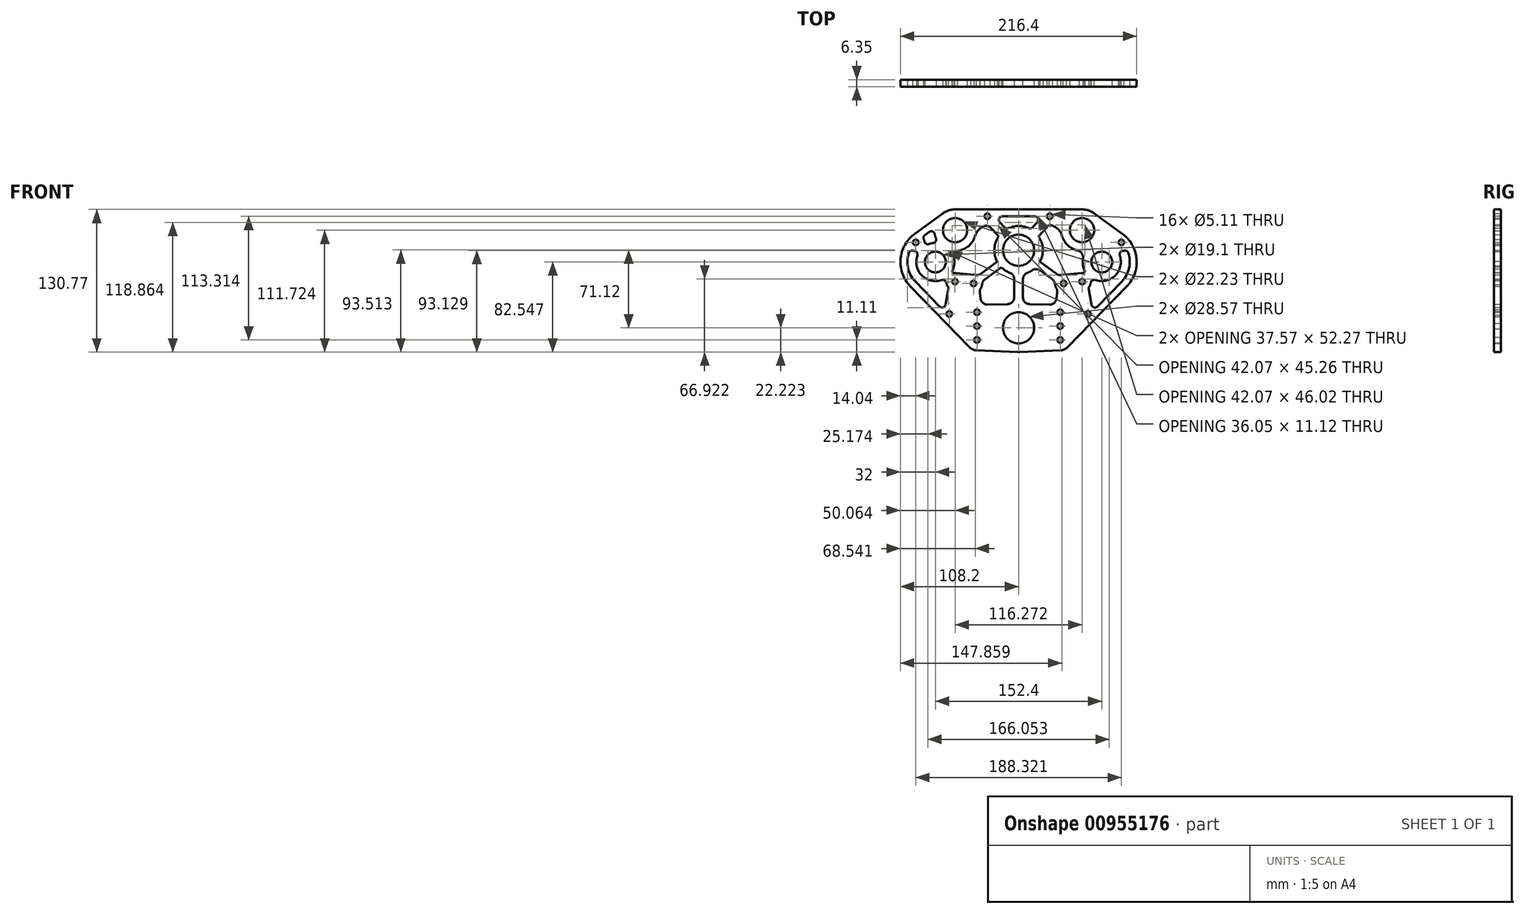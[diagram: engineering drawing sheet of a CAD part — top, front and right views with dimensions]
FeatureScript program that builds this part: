
annotation { "Feature Type Name" : "Feature", "Feature Type Description" : "" }
export const myFeature = defineFeature(function(context is Context, id is Id, definition is map)
    precondition{}
    {
        {
            var Q0;
            Q0=qCreatedBy(makeId("Front.planeOp"),FACE);
            var sketch = newSketch(context, id + "F0", { "sketchPlane" : qUnion([Q0])});
            skCircle(sketch, "E0", {"center": v(-76.2, 58.74) * mm, "radius": 32 * mm, "construction": true});
            skCircle(sketch, "E1", {"center": v(76.2, 58.74) * mm, "radius": 32 * mm, "construction": true});
            skLineSegment(sketch, "E2", {"start": v(-76.2, 58.74) * mm, "end": v(76.2, 58.74) * mm, "construction": true});
            skLineSegment(sketch, "E3", {"start": v(0, 58.74) * mm, "end": v(0, 0) * mm, "construction": true});
            skCircle(sketch, "E4", {"center": v(-76.2, 58.74) * mm, "radius": 7.63 * mm, "construction": true});
            skCircle(sketch, "E5", {"center": v(76.2, 58.74) * mm, "radius": 7.63 * mm, "construction": true});
            skLineSegment(sketch, "E6.bottom", {"start": v(-127, 23.81) * mm, "end": v(127, 23.81) * mm, "construction": true});
            skLineSegment(sketch, "E6.top", {"start": v(-127, -26.99) * mm, "end": v(127, -26.99) * mm, "construction": true});
            skLineSegment(sketch, "E6.left", {"start": v(-127, 23.81) * mm, "end": v(-127, -26.99) * mm, "construction": true});
            skLineSegment(sketch, "E6.right", {"start": v(127, 23.81) * mm, "end": v(127, -26.99) * mm, "construction": true});
            skPoint(sketch, "E6.middle", {"position": v(0, -1.59) * mm});
            skCircle(sketch, "E7", {"center": v(0, 0) * mm, "radius": 50.8 * mm, "construction": true});
            skCircle(sketch, "E8", {"center": v(-58.14, 87.91) * mm, "radius": 26.68 * mm, "construction": true});
            skCircle(sketch, "E9", {"center": v(58.14, 87.91) * mm, "radius": 26.68 * mm, "construction": true});
            skCircle(sketch, "E10", {"center": v(0, 69.53) * mm, "radius": 34.3 * mm, "construction": true});
            skCircle(sketch, "E11", {"center": v(0, 69.53) * mm, "radius": 25.4 * mm, "construction": true});
            skCircle(sketch, "E12", {"center": v(0, 69.53) * mm, "radius": 38.1 * mm, "construction": true});
            skCircle(sketch, "E13", {"center": v(0, -1.59) * mm, "radius": 33.02 * mm, "construction": true});
            skCircle(sketch, "E14", {"center": v(0, -1.59) * mm, "radius": 45.72 * mm, "construction": true});
            skCircle(sketch, "E15", {"center": v(-76.2, 58.74) * mm, "radius": 9.55 * mm});
            skCircle(sketch, "E16", {"center": v(76.2, 58.74) * mm, "radius": 9.55 * mm});
            skCircle(sketch, "E17", {"center": v(-58.14, 87.91) * mm, "radius": 11.11 * mm});
            skCircle(sketch, "E18", {"center": v(58.14, 87.91) * mm, "radius": 11.11 * mm});
            skCircle(sketch, "E19", {"center": v(0, 69.53) * mm, "radius": 14.29 * mm});
            skCircle(sketch, "E20", {"center": v(0, -1.59) * mm, "radius": 14.29 * mm});
            skCircle(sketch, "E21", {"center": v(-38.1, 12.7) * mm, "radius": 9.53 * mm, "construction": true});
            skCircle(sketch, "E22", {"center": v(-38.1, -12.7) * mm, "radius": 9.53 * mm, "construction": true});
            skCircle(sketch, "E23", {"center": v(38.1, -12.7) * mm, "radius": 9.53 * mm, "construction": true});
            skCircle(sketch, "E24", {"center": v(38.1, 12.7) * mm, "radius": 9.53 * mm, "construction": true});
            skCircle(sketch, "E25", {"center": v(38.1, 0) * mm, "radius": 9.53 * mm, "construction": true});
            skCircle(sketch, "E26", {"center": v(-38.1, 0) * mm, "radius": 9.53 * mm, "construction": true});
            skCircle(sketch, "E27", {"center": v(38.1, -12.7) * mm, "radius": 2.55 * mm});
            skCircle(sketch, "E28", {"center": v(38.1, 0) * mm, "radius": 2.55 * mm});
            skCircle(sketch, "E29", {"center": v(38.1, 12.7) * mm, "radius": 2.55 * mm});
            skCircle(sketch, "E30", {"center": v(-38.1, 12.7) * mm, "radius": 2.55 * mm});
            skCircle(sketch, "E31", {"center": v(-38.1, 0) * mm, "radius": 2.55 * mm});
            skCircle(sketch, "E32", {"center": v(-38.1, -12.7) * mm, "radius": 2.55 * mm});
            skLineSegment(sketch, "E33", {"start": v(-44.93, -19.34) * mm, "end": v(-99.15, 36.43) * mm});
            skArc(sketch, "E34", {"start": v(-44.93, -19.34) * mm, "mid": v(-42, -21.4) * mm, "end": v(-38.5, -22.22) * mm});
            skArc(sketch, "E35", {"start": v(38.5, -22.22) * mm, "mid": v(42, -21.4) * mm, "end": v(44.93, -19.34) * mm});
            skLineSegment(sketch, "E36", {"start": v(44.93, -19.34) * mm, "end": v(99.15, 36.43) * mm});
            skCircle(sketch, "E37", {"center": v(58.14, 87.91) * mm, "radius": 19.05 * mm, "construction": true});
            skCircle(sketch, "E38", {"center": v(-58.14, 87.91) * mm, "radius": 19.05 * mm, "construction": true});
            skArc(sketch, "E39", {"start": v(99.15, 36.43) * mm, "mid": v(108.09, 61.46) * mm, "end": v(95.04, 84.61) * mm});
            skArc(sketch, "E40", {"start": v(-95.04, 84.61) * mm, "mid": v(-108.09, 61.46) * mm, "end": v(-99.15, 36.43) * mm});
            skLineSegment(sketch, "E41", {"start": v(-58.24, 40.78) * mm, "end": v(-76.2, 58.74) * mm, "construction": true});
            skLineSegment(sketch, "E42", {"start": v(-76.2, 58.74) * mm, "end": v(-94.16, 76.7) * mm, "construction": true});
            skCircle(sketch, "E43", {"center": v(-94.16, 76.7) * mm, "radius": 2.55 * mm});
            skCircle(sketch, "E44", {"center": v(-58.24, 40.78) * mm, "radius": 2.55 * mm});
            skCircle(sketch, "E45.MirrorC", {"center": v(58.24, 40.78) * mm, "radius": 2.55 * mm});
            skLineSegment(sketch, "E46.MirrorCS", {"start": v(58.24, 40.78) * mm, "end": v(76.2, 58.74) * mm, "construction": true});
            skLineSegment(sketch, "E47.MirrorCS", {"start": v(76.2, 58.74) * mm, "end": v(94.16, 76.7) * mm, "construction": true});
            skCircle(sketch, "E48.MirrorC", {"center": v(94.16, 76.7) * mm, "radius": 2.55 * mm});
            skLineSegment(sketch, "E49", {"start": v(95.04, 84.61) * mm, "end": v(69.35, 103.31) * mm});
            skLineSegment(sketch, "E50", {"start": v(-95.04, 84.61) * mm, "end": v(-69.35, 103.31) * mm});
            skLineSegment(sketch, "E51", {"start": v(-58.14, 106.96) * mm, "end": v(58.14, 106.96) * mm});
            skArc(sketch, "E52", {"start": v(-69.35, 103.31) * mm, "mid": v(-64.03, 106.03) * mm, "end": v(-58.14, 106.96) * mm});
            skArc(sketch, "E53", {"start": v(58.14, 106.96) * mm, "mid": v(64.03, 106.03) * mm, "end": v(69.35, 103.31) * mm});
            skCircle(sketch, "E54", {"center": v(0, -1.59) * mm, "radius": 22.23 * mm, "construction": true});
            skLineSegment(sketch, "E55", {"start": v(38.5, -22.22) * mm, "end": v(0.93, -23.8) * mm});
            skLineSegment(sketch, "E56", {"start": v(-38.5, -22.22) * mm, "end": v(-0.93, -23.8) * mm});
            skArc(sketch, "E57", {"start": v(-0.93, -23.8) * mm, "mid": v(0, -23.81) * mm, "end": v(0.93, -23.8) * mm});
            skLineSegment(sketch, "E58.bottom", {"start": v(-38.1, -12.7) * mm, "end": v(38.1, -12.7) * mm, "construction": true});
            skLineSegment(sketch, "E58.top", {"start": v(-38.1, 12.7) * mm, "end": v(38.1, 12.7) * mm, "construction": true});
            skLineSegment(sketch, "E58.left", {"start": v(-38.1, -12.7) * mm, "end": v(-38.1, 12.7) * mm, "construction": true});
            skLineSegment(sketch, "E58.right", {"start": v(38.1, -12.7) * mm, "end": v(38.1, 12.7) * mm, "construction": true});
            skCircle(sketch, "E59", {"center": v(-28.58, 100.61) * mm, "radius": 6.35 * mm, "construction": true});
            skCircle(sketch, "E60", {"center": v(-28.58, 100.61) * mm, "radius": 2.55 * mm});
            skCircle(sketch, "E61.MirrorC", {"center": v(28.57, 100.61) * mm, "radius": 6.35 * mm, "construction": true});
            skCircle(sketch, "E62.MirrorC", {"center": v(28.57, 100.61) * mm, "radius": 2.55 * mm});
            skCircle(sketch, "E63", {"center": v(-63.5, 11.15) * mm, "radius": 7.94 * mm, "construction": true});
            skCircle(sketch, "E64", {"center": v(-63.5, 11.15) * mm, "radius": 2.55 * mm});
            skCircle(sketch, "E65.MirrorC", {"center": v(63.5, 11.15) * mm, "radius": 7.94 * mm, "construction": true});
            skCircle(sketch, "E66.MirrorC", {"center": v(63.5, 11.15) * mm, "radius": 2.55 * mm});
            skCircle(sketch, "E67", {"center": v(-41.28, 39.05) * mm, "radius": 6.35 * mm, "construction": true});
            skCircle(sketch, "E68", {"center": v(41.28, 39.05) * mm, "radius": 6.35 * mm, "construction": true});
            skCircle(sketch, "E69", {"center": v(41.28, 39.05) * mm, "radius": 2.55 * mm});
            skCircle(sketch, "E70", {"center": v(-41.28, 39.05) * mm, "radius": 2.55 * mm});
            skLineSegment(sketch, "E71", {"start": v(41.28, 39.05) * mm, "end": v(-41.28, 39.05) * mm, "construction": true});
            skLineSegment(sketch, "E72", {"start": v(0, 39.05) * mm, "end": v(0, 69.53) * mm, "construction": true});
            skSolve(sketch);
        }
        {
            var Q0;
            Q0=qSketchRegion(id+"F0",true);
            extrude(context, id + "F1", {"entities" : qUnion([Q0]), "depth" : 6.35 * mm, "offsetDistance" : 25.4 * mm});
        }
        {
            var Q0;
            Q0=makeQuery(id+"F1.opExtrude","CAP_FACE",FACE,{"disambiguationData":[OSD([sQuery(id+"F0.wireOp",EDGE,"E15"),sQuery(id+"F0.wireOp",EDGE,"E16"),sQuery(id+"F0.wireOp",EDGE,"E17"),sQuery(id+"F0.wireOp",EDGE,"E18"),sQuery(id+"F0.wireOp",EDGE,"E19"),sQuery(id+"F0.wireOp",EDGE,"E20"),sQuery(id+"F0.wireOp",EDGE,"E27"),sQuery(id+"F0.wireOp",EDGE,"E28"),sQuery(id+"F0.wireOp",EDGE,"E29"),sQuery(id+"F0.wireOp",EDGE,"E30"),sQuery(id+"F0.wireOp",EDGE,"E31"),sQuery(id+"F0.wireOp",EDGE,"E32"),sQuery(id+"F0.wireOp",EDGE,"E33"),sQuery(id+"F0.wireOp",EDGE,"E34"),sQuery(id+"F0.wireOp",EDGE,"E35"),sQuery(id+"F0.wireOp",EDGE,"E36"),sQuery(id+"F0.wireOp",EDGE,"E39"),sQuery(id+"F0.wireOp",EDGE,"E40"),sQuery(id+"F0.wireOp",EDGE,"E43"),sQuery(id+"F0.wireOp",EDGE,"E44"),sQuery(id+"F0.wireOp",EDGE,"E45.MirrorC"),sQuery(id+"F0.wireOp",EDGE,"E48.MirrorC"),sQuery(id+"F0.wireOp",EDGE,"E49"),sQuery(id+"F0.wireOp",EDGE,"E50"),sQuery(id+"F0.wireOp",EDGE,"E51"),sQuery(id+"F0.wireOp",EDGE,"E52"),sQuery(id+"F0.wireOp",EDGE,"E53"),sQuery(id+"F0.wireOp",EDGE,"E55"),sQuery(id+"F0.wireOp",EDGE,"E56"),sQuery(id+"F0.wireOp",EDGE,"E57"),sQuery(id+"F0.wireOp",EDGE,"E60"),sQuery(id+"F0.wireOp",EDGE,"E62.MirrorC"),sQuery(id+"F0.wireOp",EDGE,"E64"),sQuery(id+"F0.wireOp",EDGE,"E66.MirrorC"),sQuery(id+"F0.wireOp",EDGE,"E69"),sQuery(id+"F0.wireOp",EDGE,"E70")])],"isStart":false});
            var sketch = newSketch(context, id + "F2", { "sketchPlane" : qUnion([Q0])});
            skCircle(sketch, "E73", {"center": v(-58.14, 87.91) * mm, "radius": 19.05 * mm, "construction": true});
            skCircle(sketch, "E74", {"center": v(0, 69.53) * mm, "radius": 22.23 * mm, "construction": true});
            skCircle(sketch, "E75", {"center": v(58.14, 87.91) * mm, "radius": 19.05 * mm, "construction": true});
            skCircle(sketch, "E76", {"center": v(76.2, 58.74) * mm, "radius": 17.49 * mm, "construction": true});
            skCircle(sketch, "E77", {"center": v(94.16, 76.7) * mm, "radius": 7.94 * mm, "construction": true});
            skCircle(sketch, "E78", {"center": v(58.24, 40.78) * mm, "radius": 7.94 * mm, "construction": true});
            skCircle(sketch, "E79", {"center": v(41.28, 39.05) * mm, "radius": 7.94 * mm, "construction": true});
            skCircle(sketch, "E80", {"center": v(63.5, 11.15) * mm, "radius": 7.94 * mm, "construction": true});
            skCircle(sketch, "E81", {"center": v(38.1, 12.7) * mm, "radius": 7.94 * mm, "construction": true});
            skCircle(sketch, "E82", {"center": v(38.1, 0) * mm, "radius": 7.94 * mm, "construction": true});
            skCircle(sketch, "E83", {"center": v(38.1, -12.7) * mm, "radius": 7.94 * mm, "construction": true});
            skCircle(sketch, "E84", {"center": v(-38.1, 12.7) * mm, "radius": 7.94 * mm, "construction": true});
            skCircle(sketch, "E85", {"center": v(-38.1, 0) * mm, "radius": 7.94 * mm, "construction": true});
            skCircle(sketch, "E86", {"center": v(-38.1, -12.7) * mm, "radius": 7.94 * mm, "construction": true});
            skCircle(sketch, "E87", {"center": v(-63.5, 11.15) * mm, "radius": 7.94 * mm, "construction": true});
            skCircle(sketch, "E88", {"center": v(-41.28, 39.05) * mm, "radius": 7.94 * mm, "construction": true});
            skCircle(sketch, "E89", {"center": v(-58.24, 40.78) * mm, "radius": 7.94 * mm, "construction": true});
            skCircle(sketch, "E90", {"center": v(-76.2, 58.74) * mm, "radius": 17.49 * mm, "construction": true});
            skCircle(sketch, "E91", {"center": v(-94.16, 76.7) * mm, "radius": 7.94 * mm, "construction": true});
            skCircle(sketch, "E92", {"center": v(-28.58, 100.61) * mm, "radius": 7.94 * mm, "construction": true});
            skCircle(sketch, "E93", {"center": v(28.57, 100.61) * mm, "radius": 7.94 * mm, "construction": true});
            skCircle(sketch, "E94", {"center": v(0, -1.59) * mm, "radius": 22.23 * mm, "construction": true});
            skLineSegment(sketch, "E95", {"start": v(-99.15, 36.43) * mm, "end": v(-44.93, -19.34) * mm, "construction": true});
            skLineSegment(sketch, "E96", {"start": v(-38.5, -22.22) * mm, "end": v(-0.93, -23.8) * mm, "construction": true});
            skLineSegment(sketch, "E97", {"start": v(0.93, -23.8) * mm, "end": v(38.5, -22.22) * mm, "construction": true});
            skLineSegment(sketch, "E98", {"start": v(44.93, -19.34) * mm, "end": v(99.15, 36.43) * mm, "construction": true});
            skLineSegment(sketch, "E99", {"start": v(95.04, 84.61) * mm, "end": v(69.35, 103.31) * mm, "construction": true});
            skLineSegment(sketch, "E100", {"start": v(58.14, 106.96) * mm, "end": v(-58.14, 106.96) * mm, "construction": true});
            skLineSegment(sketch, "E101", {"start": v(-69.35, 103.31) * mm, "end": v(-95.04, 84.61) * mm, "construction": true});
            skArc(sketch, "E102", {"start": v(-58.14, 106.96) * mm, "mid": v(-64.03, 106.03) * mm, "end": v(-69.35, 103.31) * mm, "construction": true});
            skArc(sketch, "E103", {"start": v(-95.04, 84.61) * mm, "mid": v(-108.09, 61.46) * mm, "end": v(-99.15, 36.43) * mm, "construction": true});
            skArc(sketch, "E104", {"start": v(-44.93, -19.34) * mm, "mid": v(-42, -21.4) * mm, "end": v(-38.5, -22.22) * mm, "construction": true});
            skArc(sketch, "E105", {"start": v(-0.93, -23.8) * mm, "mid": v(0, -23.81) * mm, "end": v(0.93, -23.8) * mm, "construction": true});
            skArc(sketch, "E106", {"start": v(38.5, -22.22) * mm, "mid": v(42, -21.4) * mm, "end": v(44.93, -19.34) * mm, "construction": true});
            skArc(sketch, "E107", {"start": v(99.15, 36.43) * mm, "mid": v(108.09, 61.46) * mm, "end": v(95.04, 84.61) * mm, "construction": true});
            skLineSegment(sketch, "E108.0", {"start": v(58.14, 100.61) * mm, "end": v(-58.14, 100.61) * mm, "construction": true});
            skArc(sketch, "E108.1", {"start": v(58.14, 100.61) * mm, "mid": v(62.07, 99.99) * mm, "end": v(65.61, 98.18) * mm, "construction": true});
            skLineSegment(sketch, "E108.2", {"start": v(91.3, 79.48) * mm, "end": v(65.61, 98.18) * mm, "construction": true});
            skArc(sketch, "E108.3", {"start": v(-40.38, -14.91) * mm, "mid": v(-39.4, -15.6) * mm, "end": v(-38.23, -15.87) * mm, "construction": true});
            skLineSegment(sketch, "E108.4", {"start": v(-94.6, 40.85) * mm, "end": v(-40.38, -14.91) * mm, "construction": true});
            skArc(sketch, "E108.5", {"start": v(-91.3, 79.48) * mm, "mid": v(-101.76, 60.92) * mm, "end": v(-94.6, 40.85) * mm, "construction": true});
            skLineSegment(sketch, "E108.6", {"start": v(-65.61, 98.18) * mm, "end": v(-91.3, 79.48) * mm, "construction": true});
            skLineSegment(sketch, "E108.7", {"start": v(-38.23, -15.87) * mm, "end": v(-0.67, -17.45) * mm, "construction": true});
            skArc(sketch, "E108.8", {"start": v(-0.67, -17.45) * mm, "mid": v(0, -17.46) * mm, "end": v(0.67, -17.45) * mm, "construction": true});
            skLineSegment(sketch, "E108.9", {"start": v(0.67, -17.45) * mm, "end": v(38.23, -15.87) * mm, "construction": true});
            skArc(sketch, "E108.10", {"start": v(-58.14, 100.61) * mm, "mid": v(-62.07, 99.99) * mm, "end": v(-65.61, 98.18) * mm, "construction": true});
            skArc(sketch, "E108.11", {"start": v(38.23, -15.87) * mm, "mid": v(39.4, -15.6) * mm, "end": v(40.38, -14.91) * mm, "construction": true});
            skLineSegment(sketch, "E108.12", {"start": v(40.38, -14.91) * mm, "end": v(94.6, 40.85) * mm, "construction": true});
            skArc(sketch, "E108.13", {"start": v(94.6, 40.85) * mm, "mid": v(101.76, 60.92) * mm, "end": v(91.3, 79.48) * mm, "construction": true});
            skArc(sketch, "E109", {"start": v(-59, 61.93) * mm, "mid": v(-58.88, 56.32) * mm, "end": v(-60.53, 50.97) * mm});
            skArc(sketch, "E110", {"start": v(-58.97, 48.68) * mm, "mid": v(-58.2, 48.71) * mm, "end": v(-57.44, 48.67) * mm});
            skLineSegment(sketch, "E111", {"start": v(-57.44, 48.67) * mm, "end": v(-40.47, 46.95) * mm});
            skLineSegment(sketch, "E112", {"start": v(-41.28, 39.05) * mm, "end": v(0, 69.53) * mm, "construction": true});
            skLineSegment(sketch, "E113", {"start": v(-34.6, 47.93) * mm, "end": v(-19.58, 59.02) * mm});
            skLineSegment(sketch, "E114", {"start": v(-33.54, 40.82) * mm, "end": v(-15.8, 53.91) * mm});
            skLineSegment(sketch, "E115", {"start": v(-28.45, 52.47) * mm, "end": v(-26.56, 49.92) * mm, "construction": true});
            skLineSegment(sketch, "E116", {"start": v(-24.67, 47.37) * mm, "end": v(-26.56, 49.92) * mm, "construction": true});
            skArc(sketch, "E117", {"start": v(-40.47, 46.95) * mm, "mid": v(-40.06, 46.9) * mm, "end": v(-39.66, 46.82) * mm});
            skArc(sketch, "E118", {"start": v(-19.58, 59.02) * mm, "mid": v(-22.21, 70.25) * mm, "end": v(-18.86, 81.3) * mm});
            skLineSegment(sketch, "E119", {"start": v(0, 69.53) * mm, "end": v(-28.58, 100.61) * mm, "construction": true});
            skLineSegment(sketch, "E120", {"start": v(-19.04, 83.2) * mm, "end": v(-25.2, 89.9) * mm});
            skArc(sketch, "E121", {"start": v(-32.76, 91.25) * mm, "mid": v(-37.18, 87.69) * mm, "end": v(-39.82, 82.66) * mm});
            skArc(sketch, "E122", {"start": v(-54.1, 69.3) * mm, "mid": v(-45.12, 74) * mm, "end": v(-39.82, 82.66) * mm});
            skPoint(sketch, "E123.visualSharp", {"position": v(-62.28, 69.32) * mm});
            skArc(sketch, "E123.filletArc", {"start": v(-54.1, 69.3) * mm, "mid": v(-58.05, 66.6) * mm, "end": v(-59, 61.93) * mm});
            skPoint(sketch, "E124.visualSharp", {"position": v(-37.3, 45.93) * mm});
            skArc(sketch, "E124.filletArc", {"start": v(-39.66, 46.82) * mm, "mid": v(-37, 46.84) * mm, "end": v(-34.6, 47.93) * mm});
            skPoint(sketch, "E125.visualSharp", {"position": v(-63.47, 46.75) * mm});
            skArc(sketch, "E125.filletArc", {"start": v(-60.53, 50.97) * mm, "mid": v(-60.42, 49.36) * mm, "end": v(-58.97, 48.68) * mm});
            skPoint(sketch, "E126.visualSharp", {"position": v(-18.2, 82.3) * mm});
            skArc(sketch, "E126.filletArc", {"start": v(-18.86, 81.3) * mm, "mid": v(-18.63, 82.28) * mm, "end": v(-19.04, 83.2) * mm});
            skLineSegment(sketch, "E127", {"start": v(0, 69.53) * mm, "end": v(0, 0) * mm, "construction": true});
            skArc(sketch, "E128.MirrorCS", {"start": v(58.97, 48.68) * mm, "mid": v(58.2, 48.71) * mm, "end": v(57.44, 48.67) * mm});
            skArc(sketch, "E129.MirrorCS", {"start": v(60.53, 50.97) * mm, "mid": v(60.42, 49.36) * mm, "end": v(58.97, 48.68) * mm});
            skArc(sketch, "E130.MirrorCS", {"start": v(18.86, 81.3) * mm, "mid": v(18.63, 82.28) * mm, "end": v(19.04, 83.2) * mm});
            skLineSegment(sketch, "E131.MirrorCS", {"start": v(28.45, 52.47) * mm, "end": v(26.56, 49.92) * mm, "construction": true});
            skArc(sketch, "E132.MirrorCS", {"start": v(40.47, 46.95) * mm, "mid": v(40.06, 46.9) * mm, "end": v(39.66, 46.82) * mm});
            skArc(sketch, "E133.MirrorCS", {"start": v(39.66, 46.82) * mm, "mid": v(37, 46.84) * mm, "end": v(34.6, 47.93) * mm});
            skLineSegment(sketch, "E134.MirrorCS", {"start": v(24.67, 47.37) * mm, "end": v(26.56, 49.92) * mm, "construction": true});
            skArc(sketch, "E135.MirrorCS", {"start": v(54.1, 69.3) * mm, "mid": v(45.12, 74) * mm, "end": v(39.82, 82.66) * mm});
            skArc(sketch, "E136.MirrorCS", {"start": v(19.58, 59.02) * mm, "mid": v(22.21, 70.25) * mm, "end": v(18.86, 81.3) * mm});
            skPoint(sketch, "E137.MirrorP", {"position": v(37.3, 45.93) * mm});
            skLineSegment(sketch, "E138.MirrorCS", {"start": v(57.44, 48.67) * mm, "end": v(40.47, 46.95) * mm});
            skArc(sketch, "E139.MirrorCS", {"start": v(27.78, 92.72) * mm, "mid": v(35.35, 89.54) * mm, "end": v(39.82, 82.66) * mm});
            skLineSegment(sketch, "E140.MirrorCS", {"start": v(33.54, 40.82) * mm, "end": v(15.8, 53.91) * mm});
            skPoint(sketch, "E141.MirrorP", {"position": v(63.47, 46.75) * mm});
            skLineSegment(sketch, "E142.MirrorCS", {"start": v(34.6, 47.93) * mm, "end": v(19.58, 59.02) * mm});
            skArc(sketch, "E143.MirrorCS", {"start": v(54.1, 69.3) * mm, "mid": v(58.05, 66.6) * mm, "end": v(59, 61.93) * mm});
            skLineSegment(sketch, "E144.MirrorCS", {"start": v(19.04, 83.2) * mm, "end": v(27.78, 92.72) * mm});
            skPoint(sketch, "E145.MirrorP", {"position": v(18.2, 82.3) * mm});
            skArc(sketch, "E146.MirrorCS", {"start": v(59, 61.93) * mm, "mid": v(58.88, 56.32) * mm, "end": v(60.53, 50.97) * mm});
            skLineSegment(sketch, "E147.MirrorCS", {"start": v(-58.14, 100.61) * mm, "end": v(58.14, 100.61) * mm, "construction": true});
            skPoint(sketch, "E148.MirrorP", {"position": v(62.28, 69.32) * mm});
            skLineSegment(sketch, "E149", {"start": v(-11.19, 88.74) * mm, "end": v(-20.77, 99.16) * mm, "construction": true});
            skLineSegment(sketch, "E150", {"start": v(11.19, 88.74) * mm, "end": v(20.77, 99.16) * mm, "construction": true});
            skArc(sketch, "E151", {"start": v(-9.18, 89.77) * mm, "mid": v(0, 91.76) * mm, "end": v(9.18, 89.77) * mm});
            skLineSegment(sketch, "E152", {"start": v(0, 69.53) * mm, "end": v(28.57, 100.61) * mm, "construction": true});
            skLineSegment(sketch, "E153", {"start": v(0, 69.53) * mm, "end": v(41.28, 39.05) * mm, "construction": true});
            skLineSegment(sketch, "E154", {"start": v(-14.87, 100.61) * mm, "end": v(14.87, 100.61) * mm});
            skLineSegment(sketch, "E155", {"start": v(12.82, 90.52) * mm, "end": v(17.21, 95.29) * mm});
            skLineSegment(sketch, "E156", {"start": v(-12.82, 90.52) * mm, "end": v(-17.21, 95.29) * mm});
            skPoint(sketch, "E157.visualSharp", {"position": v(-22.1, 100.61) * mm});
            skArc(sketch, "E157.filletArc", {"start": v(-14.87, 100.61) * mm, "mid": v(-17.78, 98.71) * mm, "end": v(-17.21, 95.29) * mm});
            skPoint(sketch, "E158.visualSharp", {"position": v(-11.19, 88.74) * mm});
            skArc(sketch, "E158.filletArc", {"start": v(-12.82, 90.52) * mm, "mid": v(-11.12, 89.56) * mm, "end": v(-9.18, 89.77) * mm});
            skPoint(sketch, "E159.visualSharp", {"position": v(11.19, 88.74) * mm});
            skArc(sketch, "E159.filletArc", {"start": v(9.18, 89.77) * mm, "mid": v(11.12, 89.56) * mm, "end": v(12.82, 90.52) * mm});
            skPoint(sketch, "E160.visualSharp", {"position": v(22.1, 100.61) * mm});
            skArc(sketch, "E160.filletArc", {"start": v(17.21, 95.29) * mm, "mid": v(17.78, 98.71) * mm, "end": v(14.87, 100.61) * mm});
            skArc(sketch, "E161", {"start": v(-96.5, 69.12) * mm, "mid": v(-95.87, 68.95) * mm, "end": v(-95.23, 68.83) * mm});
            skArc(sketch, "E162", {"start": v(-92.67, 64.62) * mm, "mid": v(-88.57, 46.37) * mm, "end": v(-70.32, 42.27) * mm});
            skLineSegment(sketch, "E163", {"start": v(-58.24, 40.78) * mm, "end": v(-63.5, 11.15) * mm, "construction": true});
            skLineSegment(sketch, "E164", {"start": v(-64.29, 33.95) * mm, "end": v(-66.83, 19.64) * mm});
            skArc(sketch, "E165", {"start": v(-64.8, 36.3) * mm, "mid": v(-65.65, 37.93) * mm, "end": v(-66.1, 39.7) * mm});
            skArc(sketch, "E166", {"start": v(-68.16, 17.57) * mm, "mid": v(-68.14, 17.6) * mm, "end": v(-68.11, 17.6) * mm});
            skLineSegment(sketch, "E167", {"start": v(-72.3, 17.93) * mm, "end": v(-94.6, 40.85) * mm});
            skArc(sketch, "E168", {"start": v(-100.45, 67.12) * mm, "mid": v(-101.24, 53.16) * mm, "end": v(-94.6, 40.85) * mm});
            skPoint(sketch, "E169.visualSharp", {"position": v(-99.03, 70.43) * mm});
            skArc(sketch, "E169.filletArc", {"start": v(-96.5, 69.12) * mm, "mid": v(-98.88, 68.91) * mm, "end": v(-100.45, 67.12) * mm});
            skPoint(sketch, "E170.visualSharp", {"position": v(-88.93, 70.73) * mm});
            skArc(sketch, "E170.filletArc", {"start": v(-92.67, 64.62) * mm, "mid": v(-92.95, 67.34) * mm, "end": v(-95.23, 68.83) * mm});
            skPoint(sketch, "E171.visualSharp", {"position": v(-64.21, 46) * mm});
            skArc(sketch, "E171.filletArc", {"start": v(-66.1, 39.7) * mm, "mid": v(-67.6, 42) * mm, "end": v(-70.32, 42.27) * mm});
            skPoint(sketch, "E172.visualSharp", {"position": v(-64.04, 35.36) * mm});
            skArc(sketch, "E172.filletArc", {"start": v(-64.29, 33.95) * mm, "mid": v(-64.31, 35.17) * mm, "end": v(-64.8, 36.3) * mm});
            skPoint(sketch, "E173.visualSharp", {"position": v(-67.08, 18.23) * mm});
            skArc(sketch, "E173.filletArc", {"start": v(-68.11, 17.6) * mm, "mid": v(-67.27, 18.5) * mm, "end": v(-66.83, 19.64) * mm});
            skPoint(sketch, "E174.visualSharp", {"position": v(-70.06, 15.62) * mm});
            skArc(sketch, "E174.filletArc", {"start": v(-72.3, 17.93) * mm, "mid": v(-70.3, 16.98) * mm, "end": v(-68.16, 17.57) * mm});
            skArc(sketch, "E175.MirrorCS", {"start": v(68.16, 17.57) * mm, "mid": v(68.14, 17.6) * mm, "end": v(68.11, 17.6) * mm});
            skArc(sketch, "E176.MirrorCS", {"start": v(68.11, 17.6) * mm, "mid": v(67.27, 18.5) * mm, "end": v(66.83, 19.64) * mm});
            skArc(sketch, "E177.MirrorCS", {"start": v(96.5, 69.12) * mm, "mid": v(95.87, 68.95) * mm, "end": v(95.23, 68.83) * mm});
            skArc(sketch, "E178.MirrorCS", {"start": v(64.29, 33.95) * mm, "mid": v(64.31, 35.17) * mm, "end": v(64.8, 36.3) * mm});
            skArc(sketch, "E179.MirrorCS", {"start": v(64.8, 36.3) * mm, "mid": v(65.65, 37.93) * mm, "end": v(66.1, 39.7) * mm});
            skArc(sketch, "E180.MirrorCS", {"start": v(72.3, 17.93) * mm, "mid": v(70.3, 16.98) * mm, "end": v(68.16, 17.57) * mm});
            skArc(sketch, "E181.MirrorCS", {"start": v(92.67, 64.62) * mm, "mid": v(92.95, 67.34) * mm, "end": v(95.23, 68.83) * mm});
            skArc(sketch, "E182.MirrorCS", {"start": v(96.5, 69.12) * mm, "mid": v(98.88, 68.91) * mm, "end": v(100.45, 67.12) * mm});
            skPoint(sketch, "E183.MirrorP", {"position": v(64.21, 46) * mm});
            skLineSegment(sketch, "E184.MirrorCS", {"start": v(72.3, 17.93) * mm, "end": v(94.6, 40.85) * mm});
            skPoint(sketch, "E185.MirrorP", {"position": v(70.06, 15.62) * mm});
            skPoint(sketch, "E186.MirrorP", {"position": v(99.03, 70.43) * mm});
            skArc(sketch, "E187.MirrorCS", {"start": v(100.45, 67.12) * mm, "mid": v(101.24, 53.16) * mm, "end": v(94.6, 40.85) * mm});
            skLineSegment(sketch, "E188.MirrorCS", {"start": v(64.29, 33.95) * mm, "end": v(66.83, 19.64) * mm});
            skPoint(sketch, "E189.MirrorP", {"position": v(88.93, 70.73) * mm});
            skPoint(sketch, "E190.MirrorP", {"position": v(64.04, 35.36) * mm});
            skPoint(sketch, "E191.MirrorP", {"position": v(67.08, 18.23) * mm});
            skArc(sketch, "E192.MirrorCS", {"start": v(92.67, 64.62) * mm, "mid": v(88.57, 46.37) * mm, "end": v(70.32, 42.27) * mm});
            skArc(sketch, "E193.MirrorCS", {"start": v(66.1, 39.7) * mm, "mid": v(67.6, 42) * mm, "end": v(70.32, 42.27) * mm});
            skPoint(sketch, "E194.visualSharp", {"position": v(-27.78, 92.72) * mm});
            skArc(sketch, "E194.filletArc", {"start": v(-25.2, 89.9) * mm, "mid": v(-28.75, 91.85) * mm, "end": v(-32.76, 91.25) * mm});
            skLineSegment(sketch, "E195", {"start": v(-85.76, 83.51) * mm, "end": v(-81.84, 86.36) * mm});
            skArc(sketch, "E196", {"start": v(-76.86, 84.38) * mm, "mid": v(-76.37, 82.4) * mm, "end": v(-75.68, 80.5) * mm});
            skArc(sketch, "E197", {"start": v(-78.24, 76.1) * mm, "mid": v(-80.18, 75.77) * mm, "end": v(-82.08, 75.2) * mm});
            skArc(sketch, "E198", {"start": v(-86.83, 79.73) * mm, "mid": v(-86.5, 78.77) * mm, "end": v(-86.3, 77.77) * mm});
            skPoint(sketch, "E199.visualSharp", {"position": v(-88.1, 81.81) * mm});
            skArc(sketch, "E199.filletArc", {"start": v(-85.76, 83.51) * mm, "mid": v(-86.95, 81.8) * mm, "end": v(-86.83, 79.73) * mm});
            skPoint(sketch, "E200.visualSharp", {"position": v(-72.93, 75.92) * mm});
            skArc(sketch, "E200.filletArc", {"start": v(-78.24, 76.1) * mm, "mid": v(-75.86, 77.66) * mm, "end": v(-75.68, 80.5) * mm});
            skPoint(sketch, "E201.visualSharp", {"position": v(-88.19, 71.47) * mm});
            skArc(sketch, "E201.filletArc", {"start": v(-86.3, 77.77) * mm, "mid": v(-84.8, 75.48) * mm, "end": v(-82.08, 75.2) * mm});
            skPoint(sketch, "E202.visualSharp", {"position": v(-77.1, 89.82) * mm});
            skArc(sketch, "E202.filletArc", {"start": v(-76.86, 84.38) * mm, "mid": v(-78.8, 86.75) * mm, "end": v(-81.84, 86.36) * mm});
            skLineSegment(sketch, "E203", {"start": v(-38.1, 12.7) * mm, "end": v(-63.5, 11.15) * mm, "construction": true});
            skLineSegment(sketch, "E204", {"start": v(-38.58, 20.62) * mm, "end": v(-63.98, 19.07) * mm, "construction": true});
            skArc(sketch, "E205", {"start": v(-63.98, 19.07) * mm, "mid": v(-63.96, 3.22) * mm, "end": v(-62.11, 18.96) * mm, "construction": true});
            skLineSegment(sketch, "E206", {"start": v(63.5, 11.15) * mm, "end": v(58.24, 40.78) * mm, "construction": true});
            skLineSegment(sketch, "E207", {"start": v(38.1, 12.7) * mm, "end": v(63.5, 11.15) * mm, "construction": true});
            skLineSegment(sketch, "E208", {"start": v(58.24, 40.78) * mm, "end": v(41.28, 39.05) * mm, "construction": true});
            skCircle(sketch, "E209.MirrorC", {"center": v(-41.27, 39.05) * mm, "radius": 7.94 * mm, "construction": true});
            skLineSegment(sketch, "E210", {"start": v(-3.97, 47.66) * mm, "end": v(-3.97, 20.28) * mm});
            skLineSegment(sketch, "E211", {"start": v(3.97, 20.28) * mm, "end": v(3.97, 47.66) * mm});
            skLineSegment(sketch, "E212", {"start": v(-3.97, 33.97) * mm, "end": v(0, 33.97) * mm, "construction": true});
            skLineSegment(sketch, "E213", {"start": v(0, 33.97) * mm, "end": v(3.97, 33.97) * mm, "construction": true});
            skArc(sketch, "E214", {"start": v(-3.97, 47.66) * mm, "mid": v(-10.37, 49.88) * mm, "end": v(-15.8, 53.91) * mm});
            skArc(sketch, "E215", {"start": v(3.97, 47.66) * mm, "mid": v(10.37, 49.88) * mm, "end": v(15.8, 53.91) * mm});
            skLineSegment(sketch, "E216", {"start": v(-41.28, 39.05) * mm, "end": v(-38.1, 12.7) * mm, "construction": true});
            skLineSegment(sketch, "E217", {"start": v(-35.79, 33.32) * mm, "end": v(-34.13, 19.57) * mm});
            skLineSegment(sketch, "E218", {"start": v(-34.13, 19.57) * mm, "end": v(-3.97, 20.28) * mm});
            skArc(sketch, "E219", {"start": v(-35.79, 33.32) * mm, "mid": v(-33.67, 36.77) * mm, "end": v(-33.54, 40.82) * mm});
            skArc(sketch, "E220", {"start": v(33.54, 40.82) * mm, "mid": v(33.67, 36.77) * mm, "end": v(35.79, 33.32) * mm});
            skLineSegment(sketch, "E221", {"start": v(35.79, 33.32) * mm, "end": v(34.13, 19.57) * mm});
            skLineSegment(sketch, "E222", {"start": v(3.97, 20.28) * mm, "end": v(34.13, 19.57) * mm});
            skArc(sketch, "E223", {"start": v(-15.8, 53.91) * mm, "mid": v(-10.37, 49.88) * mm, "end": v(-3.97, 47.66) * mm});
            skSolve(sketch);
        }
        {
            var Q0;
            Q0=qSketchRegion(id+"F2",true);
            extrude(context, id + "F3", {"entities" : qUnion([Q0]), "operationType" : NewBodyOperationType.REMOVE, "endBound" : BoundingType.THROUGH_ALL, "oppositeDirection" : true, "depth" : 25.4 * mm, "offsetDistance" : 25.4 * mm});
        }
        {
            var Q0;
            Q0=makeQuery(id+"F3.boolean.opBoolean","COPY",EDGE,{"derivedFrom":makeQuery(id+"F3.opExtrude","SWEPT_EDGE",EDGE,{"disambiguationData":[OSD([sQuery(id+"F2.wireOp",EDGE,"E114"),sQuery(id+"F2.wireOp",EDGE,"E223")])]})});
            var Q1;
            Q1=makeQuery(id+"F3.boolean.opBoolean","COPY",EDGE,{"derivedFrom":makeQuery(id+"F3.opExtrude","SWEPT_EDGE",EDGE,{"disambiguationData":[OSD([sQuery(id+"F2.wireOp",EDGE,"E114"),sQuery(id+"F2.wireOp",EDGE,"E219")])]})});
            var Q2;
            Q2=makeQuery(id+"F3.boolean.opBoolean","COPY",EDGE,{"derivedFrom":makeQuery(id+"F3.opExtrude","SWEPT_EDGE",EDGE,{"disambiguationData":[OSD([sQuery(id+"F2.wireOp",EDGE,"E217"),sQuery(id+"F2.wireOp",EDGE,"E219")])]})});
            var Q3;
            Q3=makeQuery(id+"F3.boolean.opBoolean","COPY",EDGE,{"derivedFrom":makeQuery(id+"F3.opExtrude","SWEPT_EDGE",EDGE,{"disambiguationData":[OSD([sQuery(id+"F2.wireOp",EDGE,"E210"),sQuery(id+"F2.wireOp",EDGE,"E223")])]})});
            var Q4;
            Q4=makeQuery(id+"F3.boolean.opBoolean","COPY",EDGE,{"derivedFrom":makeQuery(id+"F3.opExtrude","SWEPT_EDGE",EDGE,{"disambiguationData":[OSD([sQuery(id+"F2.wireOp",EDGE,"E210"),sQuery(id+"F2.wireOp",EDGE,"E218")])]})});
            var Q5;
            Q5=makeQuery(id+"F3.boolean.opBoolean","COPY",EDGE,{"derivedFrom":makeQuery(id+"F3.opExtrude","SWEPT_EDGE",EDGE,{"disambiguationData":[OSD([sQuery(id+"F2.wireOp",EDGE,"E217"),sQuery(id+"F2.wireOp",EDGE,"E218")])]})});
            var Q6;
            Q6=makeQuery(id+"F3.boolean.opBoolean","COPY",EDGE,{"derivedFrom":makeQuery(id+"F3.opExtrude","SWEPT_EDGE",EDGE,{"disambiguationData":[OSD([sQuery(id+"F2.wireOp",EDGE,"E211"),sQuery(id+"F2.wireOp",EDGE,"E222")])]})});
            var Q7;
            Q7=makeQuery(id+"F3.boolean.opBoolean","COPY",EDGE,{"derivedFrom":makeQuery(id+"F3.opExtrude","SWEPT_EDGE",EDGE,{"disambiguationData":[OSD([sQuery(id+"F2.wireOp",EDGE,"E211"),sQuery(id+"F2.wireOp",EDGE,"E215")])]})});
            var Q8;
            Q8=makeQuery(id+"F3.boolean.opBoolean","COPY",EDGE,{"derivedFrom":makeQuery(id+"F3.opExtrude","SWEPT_EDGE",EDGE,{"disambiguationData":[OSD([sQuery(id+"F2.wireOp",EDGE,"E140.MirrorCS"),sQuery(id+"F2.wireOp",EDGE,"E215")])]})});
            var Q9;
            Q9=makeQuery(id+"F3.boolean.opBoolean","COPY",EDGE,{"derivedFrom":makeQuery(id+"F3.opExtrude","SWEPT_EDGE",EDGE,{"disambiguationData":[OSD([sQuery(id+"F2.wireOp",EDGE,"E140.MirrorCS"),sQuery(id+"F2.wireOp",EDGE,"E220")])]})});
            var Q10;
            Q10=makeQuery(id+"F3.boolean.opBoolean","COPY",EDGE,{"derivedFrom":makeQuery(id+"F3.opExtrude","SWEPT_EDGE",EDGE,{"disambiguationData":[OSD([sQuery(id+"F2.wireOp",EDGE,"E220"),sQuery(id+"F2.wireOp",EDGE,"E221")])]})});
            var Q11;
            Q11=makeQuery(id+"F3.boolean.opBoolean","COPY",EDGE,{"derivedFrom":makeQuery(id+"F3.opExtrude","SWEPT_EDGE",EDGE,{"disambiguationData":[OSD([sQuery(id+"F2.wireOp",EDGE,"E221"),sQuery(id+"F2.wireOp",EDGE,"E222")])]})});
            fillet(context, id + "F4", {"entities" : qUnion([Q0, Q1, Q2, Q3, Q4, Q5, Q6, Q7, Q8, Q9, Q10, Q11]), "radius" : 6.35 * mm, "tangentPropagation" : true, "allowEdgeOverflow" : false});
        }
    });
